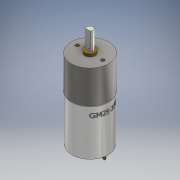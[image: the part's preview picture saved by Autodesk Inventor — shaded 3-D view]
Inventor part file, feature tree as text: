
AUTODESK INVENTOR PART (.ipt)
format: ipt  version: 2018 (Build 220112000, 112)  size: 600,064 bytes
history: native  units: mm
features: sketch x10, extrude x8, hole x3, fillet x2, plane x1, emboss x1
ambient origin geometry x8: Origin, YZ Plane, XZ Plane, XY Plane, X Axis, Y Axis, Z Axis, Center Point
bodies: Solid1 (feature_tree)
feature tree (25):
  extrude  "Extrusion1"  Depth=31.0mm TaperAngle=0.0deg
  fillet  "Fillet1"  Radius=0.8mm
  extrude  "Extrusion2"  Depth=22.0mm TaperAngle=0.0deg
  extrude  "Extrusion3"  Depth=4.1mm
  extrude  "Extrusion4"  Depth=4.0mm
  extrude  "Extrusion5"  Depth=3.4mm
  hole  "Hole1"  [1 undecoded]
  extrude  "Extrusion6"  Depth=17.0mm
  extrude  "Extrusion7"  Depth=23.4mm
  extrude  "Extrusion8"  Depth=10.0mm
  fillet  "Fillet2"  Radius=3.0mm
  hole  "Hole2"  [1 undecoded]
  hole  "Hole3"  [1 undecoded]
  plane  "Work Plane1"
  emboss  "Emboss1"
  sketch  "Sketch1"  dims[d0=24.0mm d1=31.0mm d2=0.0mm d3=0.8mm]
  sketch  "Sketch2"  dims[d4=25.0mm d5=22.0mm d6=0.0mm]
  sketch  "Sketch3"  dims[d7=7.0mm d8=4.1mm]
  sketch  "Sketch4"  dims[d9=2.0mm d10=0.0mm d11=4.0mm]
  sketch  "Sketch5"  dims[d12=14.0mm d13=0.0mm d14=3.4mm]
  sketch  "Sketch6"  dims[d15=10.0mm d16=0.0mm d17=3.0mm]
  sketch  "Sketch7"  dims[d18=3.0mm d19=17.0mm]
  sketch  "Sketch8"  dims[d20=8.5mm]
  sketch  "Sketch9"  dims[d21=2.459mm d22=6.0mm d23=4.0mm d24=2.0mm d25=90.0deg d26=8.8mm d27=20.594885mm d28=23.4mm]
  sketch  "Sketch10"  dims[d29=3.0mm d30=6.0mm d31=3.0mm d32=8.0mm d33=1.5mm d34=20.0mm d36=360.0deg d38=0.4mm d39=0.0mm d40=6.5mm d41=2.5mm d42=0.0mm d43=2.0mm d44=0.4mm d45=2.0mm d46=0.4mm d47=0.5mm d48=0.2mm d49=0.2mm d50=0.5mm d51=4.0mm d52=0.0mm d53=1.0mm d54=10.0mm d55=10.0mm d56=1.0mm d57=6.0mm d58=4.0mm d59=2.0mm d60=90.0deg d61=8.8mm d62=20.594885mm d63=10.0mm d64=10.0mm d65=1.0mm d66=6.0mm d67=4.0mm d68=2.0mm d69=90.0deg d70=8.8mm d71=20.594885mm d72=0.2mm d73=0.0mm]
note: 3 required parameter values undecoded (feature->parameter linkage not recoverable at this tier; creation-order binding heuristic only, values carry confidence <= 0.55)
